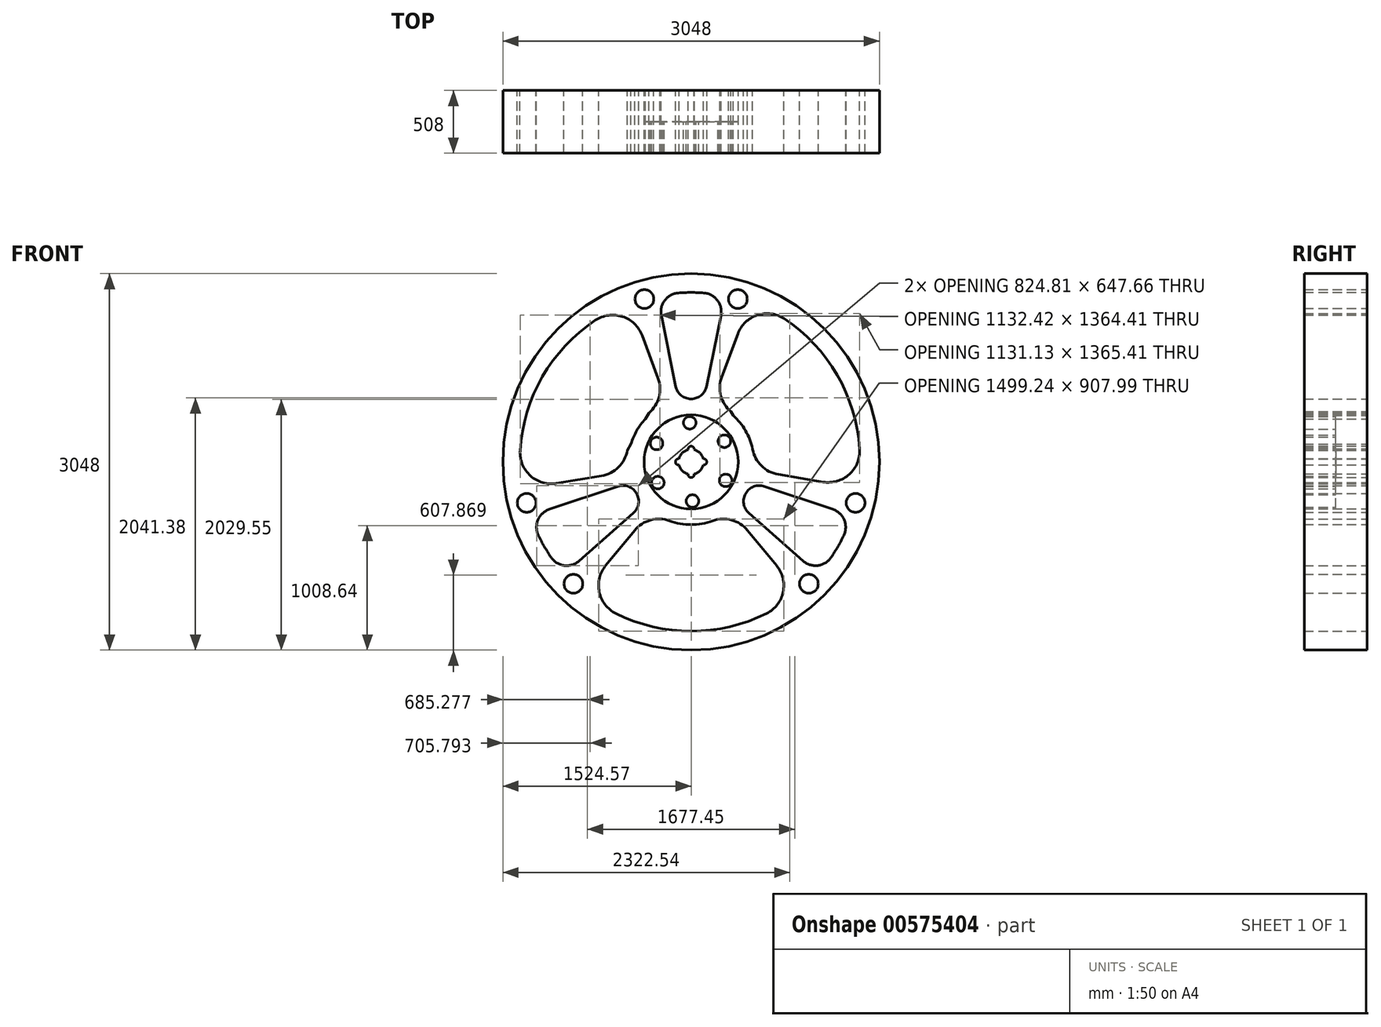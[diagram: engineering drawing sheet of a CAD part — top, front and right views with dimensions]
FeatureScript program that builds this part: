
annotation { "Feature Type Name" : "Feature", "Feature Type Description" : "" }
export const myFeature = defineFeature(function(context is Context, id is Id, definition is map)
    precondition{}
    {
        {
            var Q0;
            Q0=qCreatedBy(makeId("Front.planeOp"),FACE);
            var sketch = newSketch(context, id + "F0", { "sketchPlane" : qUnion([Q0])});
            skCircle(sketch, "E0", {"center": v(0, 0) * mm, "radius": 1524 * mm});
            skCircle(sketch, "E1", {"center": v(-378.06, 1318.47) * mm, "radius": 76.2 * mm});
            skCircle(sketch, "E2", {"center": v(378.06, 1318.47) * mm, "radius": 76.2 * mm});
            skCircle(sketch, "E3.1.0", {"center": v(-952.8, -986.65) * mm, "radius": 76.2 * mm});
            skCircle(sketch, "E3.1.1", {"center": v(-1330.86, -331.82) * mm, "radius": 76.2 * mm});
            skCircle(sketch, "E3.2.0", {"center": v(1330.86, -331.82) * mm, "radius": 76.2 * mm});
            skCircle(sketch, "E3.2.1", {"center": v(952.8, -986.65) * mm, "radius": 76.2 * mm});
            skCircle(sketch, "E4", {"center": v(0, 0) * mm, "radius": 381 * mm});
            skCircle(sketch, "E5", {"center": v(10.6, -316.87) * mm, "radius": 50.8 * mm});
            skCircle(sketch, "E6.1.0", {"center": v(279.72, -149.25) * mm, "radius": 50.8 * mm});
            skCircle(sketch, "E6.2.0", {"center": v(269.12, 167.62) * mm, "radius": 50.8 * mm});
            skCircle(sketch, "E6.3.0", {"center": v(-10.6, 316.87) * mm, "radius": 50.8 * mm});
            skCircle(sketch, "E6.4.0", {"center": v(-279.72, 149.25) * mm, "radius": 50.8 * mm});
            skCircle(sketch, "E6.5.0", {"center": v(-269.12, -167.62) * mm, "radius": 50.8 * mm});
            skArc(sketch, "E7", {"start": v(-103.3, 1367.7) * mm, "mid": v(-213.39, 1307.65) * mm, "end": v(-241.16, 1185.35) * mm});
            skArc(sketch, "E8", {"start": v(241.16, 1185.35) * mm, "mid": v(213.39, 1307.65) * mm, "end": v(103.3, 1367.7) * mm});
            skArc(sketch, "E9", {"start": v(-124.45, 611.7) * mm, "mid": v(0, 510.01) * mm, "end": v(124.45, 611.7) * mm});
            skLineSegment(sketch, "E10.trimOffspring", {"start": v(-124.45, 611.7) * mm, "end": v(-241.16, 1185.35) * mm});
            skLineSegment(sketch, "E11.trimOffspring", {"start": v(124.45, 611.7) * mm, "end": v(241.16, 1185.35) * mm});
            skArc(sketch, "E12.1.0", {"start": v(-1132.82, -773.31) * mm, "mid": v(-1025.76, -838.62) * mm, "end": v(-905.96, -801.53) * mm});
            skArc(sketch, "E12.1.1", {"start": v(-1147.13, -383.82) * mm, "mid": v(-1239.15, -469.02) * mm, "end": v(-1236.12, -594.4) * mm});
            skArc(sketch, "E12.1.2", {"start": v(-467.52, -413.62) * mm, "mid": v(-441.68, -255) * mm, "end": v(-591.97, -198.07) * mm});
            skArc(sketch, "E12.2.0", {"start": v(1236.12, -594.4) * mm, "mid": v(1239.15, -469.02) * mm, "end": v(1147.13, -383.82) * mm});
            skArc(sketch, "E12.2.1", {"start": v(905.96, -801.53) * mm, "mid": v(1025.76, -838.62) * mm, "end": v(1132.82, -773.31) * mm});
            skArc(sketch, "E12.2.2", {"start": v(591.97, -198.07) * mm, "mid": v(441.68, -255) * mm, "end": v(467.52, -413.62) * mm});
            skLineSegment(sketch, "E13", {"start": v(-905.96, -801.53) * mm, "end": v(-467.52, -413.62) * mm});
            skLineSegment(sketch, "E14", {"start": v(-1147.13, -383.82) * mm, "end": v(-591.97, -198.07) * mm});
            skLineSegment(sketch, "E15", {"start": v(467.52, -413.62) * mm, "end": v(905.96, -801.53) * mm});
            skLineSegment(sketch, "E16", {"start": v(591.97, -198.07) * mm, "end": v(1147.13, -383.82) * mm});
            skArc(sketch, "E17", {"start": v(-369.5, 348.63) * mm, "mid": v(-439.94, 254) * mm, "end": v(-486.66, 145.68) * mm});
            skLineSegment(sketch, "E18", {"start": v(0, 0) * mm, "end": v(0, -381) * mm});
            skArc(sketch, "E19.trimOffspring", {"start": v(103.3, 1367.7) * mm, "mid": v(0, 1371.6) * mm, "end": v(-103.3, 1367.7) * mm});
            skArc(sketch, "E20", {"start": v(-173.99, -477.28) * mm, "mid": v(-327.73, -470.84) * mm, "end": v(-456.97, -554.35) * mm});
            skArc(sketch, "E21", {"start": v(-691.06, -838.33) * mm, "mid": v(-743.46, -1053) * mm, "end": v(-607.86, -1227.47) * mm});
            skArc(sketch, "E22", {"start": v(456.97, -554.35) * mm, "mid": v(327.73, -470.84) * mm, "end": v(173.99, -477.28) * mm});
            skArc(sketch, "E23", {"start": v(611.38, -1226.93) * mm, "mid": v(744.86, -1052.9) * mm, "end": v(692.4, -839.95) * mm});
            skLineSegment(sketch, "E24.trimOffspring", {"start": v(0, -1371.6) * mm, "end": v(0, -1524) * mm});
            skLineSegment(sketch, "E25.trimOffspring", {"start": v(456.97, -554.35) * mm, "end": v(692.4, -839.95) * mm});
            skArc(sketch, "E26.1.0", {"start": v(497.48, 104.99) * mm, "mid": v(568.78, -31.37) * mm, "end": v(705.72, -101.55) * mm});
            skArc(sketch, "E26.1.1", {"start": v(248.75, 689.95) * mm, "mid": v(241.05, 536.27) * mm, "end": v(323.5, 406.34) * mm});
            skArc(sketch, "E26.1.2", {"start": v(1068.7, -162.29) * mm, "mid": v(1280.8, -100.33) * mm, "end": v(1364.1, 104.34) * mm});
            skArc(sketch, "E26.1.3", {"start": v(754.02, 1159.96) * mm, "mid": v(536.57, 1188.54) * mm, "end": v(378.37, 1036.64) * mm});
            skArc(sketch, "E26.2.0", {"start": v(-342.5, 395.36) * mm, "mid": v(-260.07, 525.29) * mm, "end": v(-267.77, 678.97) * mm});
            skArc(sketch, "E26.2.1", {"start": v(-724.74, -112.53) * mm, "mid": v(-587.8, -42.35) * mm, "end": v(-516.5, 94) * mm});
            skArc(sketch, "E26.2.2", {"start": v(-396.65, 1023.69) * mm, "mid": v(-556.36, 1176.4) * mm, "end": v(-775.26, 1146.2) * mm});
            skArc(sketch, "E26.2.3", {"start": v(-1384.41, 90.04) * mm, "mid": v(-1300.44, -112.57) * mm, "end": v(-1089.8, -173.62) * mm});
            skPoint(sketch, "E26.center", {"position": v(-6.34, 7.7) * mm});
            skLineSegment(sketch, "E27", {"start": v(-1089.8, -173.62) * mm, "end": v(-724.74, -112.53) * mm});
            skLineSegment(sketch, "E28", {"start": v(-396.65, 1023.69) * mm, "end": v(-267.77, 678.97) * mm});
            skLineSegment(sketch, "E29", {"start": v(378.37, 1036.64) * mm, "end": v(248.75, 689.95) * mm});
            skLineSegment(sketch, "E30", {"start": v(705.72, -101.55) * mm, "end": v(1068.7, -162.29) * mm});
            skArc(sketch, "E31.trimOffspring", {"start": v(-775.26, 1146.2) * mm, "mid": v(-1203.64, 689.53) * mm, "end": v(-1384.41, 90.04) * mm});
            skArc(sketch, "E32.trimOffspring", {"start": v(1364.1, 104.34) * mm, "mid": v(1182.8, 703.67) * mm, "end": v(754.02, 1159.96) * mm});
            skArc(sketch, "E33.trimOffspring", {"start": v(1132.82, -773.31) * mm, "mid": v(1187.84, -685.8) * mm, "end": v(1236.12, -594.4) * mm});
            skArc(sketch, "E34.trimOffspring", {"start": v(-607.86, -1227.47) * mm, "mid": v(1.82, -1370.13) * mm, "end": v(611.38, -1226.93) * mm});
            skArc(sketch, "E35.trimOffspring", {"start": v(-1236.12, -594.4) * mm, "mid": v(-1187.84, -685.8) * mm, "end": v(-1132.82, -773.31) * mm});
            skArc(sketch, "E36", {"start": v(-25.2, 98.42) * mm, "mid": v(-71.84, 71.84) * mm, "end": v(-98.43, 25.2) * mm});
            skArc(sketch, "E37", {"start": v(25.2, 98.42) * mm, "mid": v(0, 127) * mm, "end": v(-25.2, 98.43) * mm});
            skArc(sketch, "E38", {"start": v(98.42, -25.2) * mm, "mid": v(127, 0) * mm, "end": v(98.43, 25.2) * mm});
            skArc(sketch, "E39", {"start": v(-25.2, -98.42) * mm, "mid": v(0, -127) * mm, "end": v(25.2, -98.43) * mm});
            skArc(sketch, "E40", {"start": v(-98.43, 25.2) * mm, "mid": v(-127, 0) * mm, "end": v(-98.43, -25.2) * mm});
            skArc(sketch, "E41.trimOffspring", {"start": v(98.42, 25.2) * mm, "mid": v(71.84, 71.84) * mm, "end": v(25.2, 98.42) * mm});
            skArc(sketch, "E42.trimOffspring", {"start": v(25.2, -98.42) * mm, "mid": v(71.84, -71.84) * mm, "end": v(98.43, -25.2) * mm});
            skArc(sketch, "E43.trimOffspring", {"start": v(-98.42, -25.2) * mm, "mid": v(-71.84, -71.84) * mm, "end": v(-25.2, -98.43) * mm});
            skLineSegment(sketch, "E44", {"start": v(-516.5, 94) * mm, "end": v(-486.66, 145.68) * mm});
            skLineSegment(sketch, "E45", {"start": v(323.5, 406.34) * mm, "end": v(342.53, 375.15) * mm});
            skLineSegment(sketch, "E46.trimOffspring", {"start": v(-369.5, 348.63) * mm, "end": v(-342.5, 395.36) * mm});
            skArc(sketch, "E47.trimOffspring", {"start": v(-173.99, -477.28) * mm, "mid": v(0, -508) * mm, "end": v(173.99, -477.28) * mm});
            skArc(sketch, "E48.trimOffspring", {"start": v(497.17, 104.35) * mm, "mid": v(441.14, 251.9) * mm, "end": v(342.53, 375.15) * mm});
            skArc(sketch, "E49", {"start": v(496.68, 106.65) * mm, "mid": v(495.84, 105.05) * mm, "end": v(497.56, 104.51) * mm});
            skLineSegment(sketch, "E50.trimOffspring", {"start": v(-456.97, -554.35) * mm, "end": v(-691.06, -838.33) * mm});
            skLineSegment(sketch, "E51.trimOffspring", {"start": v(242.35, -293.99) * mm, "end": v(323.13, -391.99) * mm});
            skSolve(sketch);
        }
        {
            var Q0;
            Q0=makeQuery(id+"F0.imprint","IMPRINT",FACE,{"disambiguationData":[TD([[makeQuery(id+"F0.imprint","IMPRINT",EDGE,{"derivedFrom":sQuery(id+"F0.wireOp",EDGE,"E1")}),-1.0]])]});
            extrude(context, id + "F1", {"entities" : qUnion([Q0]), "depth" : 254 * mm, "offsetDistance" : 25.4 * mm});
        }
        {
            var Q0;
            Q0 = qSketchRegion(id + "F0", true);
            var Q1;
            Q1=makeQuery(id+"F0.imprint","IMPRINT",FACE,{"disambiguationData":[TD([[makeQuery(id+"F0.imprint","IMPRINT",EDGE,{"derivedFrom":sQuery(id+"F0.wireOp",EDGE,"E36")}),1.0]])]});
            extrude(context, id + "F2", {"entities" : qUnion([Q0, Q1]), "operationType" : NewBodyOperationType.ADD, "depth" : 508 * mm, "offsetDistance" : 25.4 * mm, "symmetric" : true});
        }
        {
            var Q0;
            Q0=makeQuery(id+"F0.imprint","IMPRINT",FACE,{"disambiguationData":[TD([[makeQuery(id+"F0.imprint","IMPRINT",EDGE,{"derivedFrom":sQuery(id+"F0.wireOp",EDGE,"E6.1.0")}),-1.0]])]});
            extrude(context, id + "F3", {"entities" : qUnion([Q0]), "depth" : 254 * mm, "offsetDistance" : 25.4 * mm});
        }
    });
